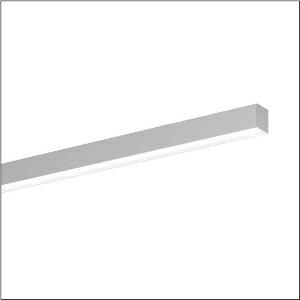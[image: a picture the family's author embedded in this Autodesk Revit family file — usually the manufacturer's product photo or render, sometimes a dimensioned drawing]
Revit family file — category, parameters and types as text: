
# Revit family: silica_r__21_51mx23db35sb_5652
name_source: partatom
category: Lighting Fixtures
units: mm (PartAtom-declared; Revit-internal decimal feet)

## family parameters
Cut with Voids When Loaded = No
Host = Face
Light Source = No
Part Type = Normal
Room Calculation Point = No
Round Connector Dimension = Use Diameter
Shared = No

## types (1)
- --- (1 x LED, 4100 lm, 30.1 W, 3000K)
    Apparent Load = 30 VA
    CIE Flux Codes = 78 96 99 100 100
    Color Rendering = 80
    Color Temperature = 3000K
    Default Elevation = 1800 mm
    Description = Silica® 21, office luminaire, primary optical cover: prismatic diffuser, of PMMA, CAT 2 (L<= 3000cd/m²), light emission: direct distribution, primary light characteristic: symmetric, installation type: surface-mounted, LED, rated luminous flux: 4.100lm, luminous efficacy: 136lm/W, light colour: 830, colour temperature: 3000K, with terminal, 3+2-pole, max. 2.5mm², mains connection: 220..240V, AC, 50/60Hz, rated input power: 30.1W, luminaire housing, of aluminium, metallic grey (RAL 9006), length: 1.504mm, width: 53mm, height: 53mm, protection rating (complete): IP20, insulation class (complete): insulation class I (protective earthing), certification: CE, permissible operating ambient temperature: 0..+35°C, standard: EN 50419, packaging unit: 1 piece
    Height = 0 mm  [stored 0 ft]
    Lamp = 1 x LED
    Lamp Light Flux = 4100 lm
    Lamp Power = 30.1 W
    Lamp count = 1
    Length = 1504 mm
    Luminous efficacy = 136 lm/W
    Manufacturer = Siteco
    ModVariant = No
    Model = 51MX23DB35SB
    Mounting Place = Ceiling
    Mounting Type = Recessed
    Number of Poles = 1
    OnlyDefault = Yes
    Power Factor = 1
    Product Name = Silica® 21
    Product group = office luminaire | ceiling recessed
    ProductGroupID = 401
    Protection Class = Protection class I
    Protection Degree = IP 20
    RLX_Detail_Level = 1
    RLX_Emergency_Light_Flux = 0 lm
    RLX_Emergency_Type = 0
    RLX_Emergency_Type_DB = No
    RlxData = <blob elided: 21289 chars, md5=9ed2490e>
    Socket = socket
    Standby Power = 0 W
    System Light Flux = 4100 lm
    System Power = 30 W
    Type Comments = factory setting: luminous flux: 100 % | dim-lin: 254 | 345 mA
    Type Image = l_1297768.jpg
    URL = http://relux.com
    VarID = @adj_049655
    Voltage = 0 V
    Weight = 0.00 kg
    Width = 53 mm

note: [stored X ft] marks values corroborated as IEEE doubles in the binary element streams (Revit-internal decimal feet)

## geometry (parser evidence)
native form markers: Blend x4, Sweep x12
no freeform markers — native parametric forms only
